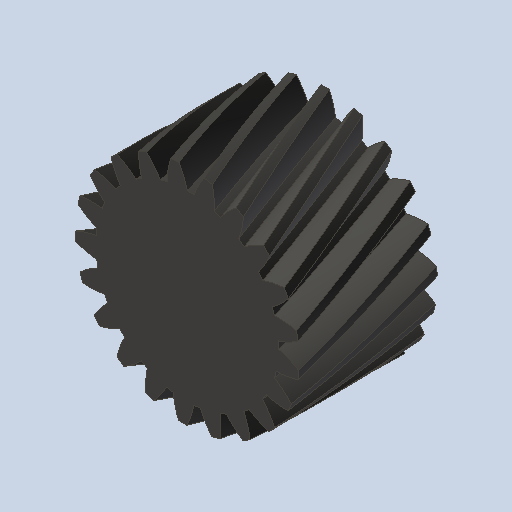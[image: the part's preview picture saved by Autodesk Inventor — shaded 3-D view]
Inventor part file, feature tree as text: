
AUTODESK INVENTOR PART (.ipt)
format: ipt  version: 2023 (Build 270158000, 158)  size: 452,608 bytes
history: native  units: mm (DEFAULTED — no unit token found)
features: plane x3, other x3, sketch x2, extrude x1
ambient origin geometry x8: Origin, YZ Plane, XZ Plane, XY Plane, X Axis, Y Axis, Z Axis, Center Point
bodies: Solid1 (feature_tree)
feature tree (9):
  extrude  "Extrusion1"  Depth=15.0mm TaperAngle=0.0deg
  plane  "Work Plane2"
  plane  "Work Plane8"
  plane  "Work Plane9"
  other  "Spur Gear"
  sketch  "Sketch1"  dims[d0=24.347678mm d1=15.0mm d2=0.0mm]
  sketch  "Sketch2"  dims[d3=22.347733mm d4=10.0mm d5=0.0mm d16=101.6mm d17=0.0mm d34=1.495997mm d39=0.0mm d41=0.0mm d43=101.6mm d46=101.6mm d47=0.0mm d48=0.0mm]
  other  "Srf1"
  other  "Pitch Diameter"
